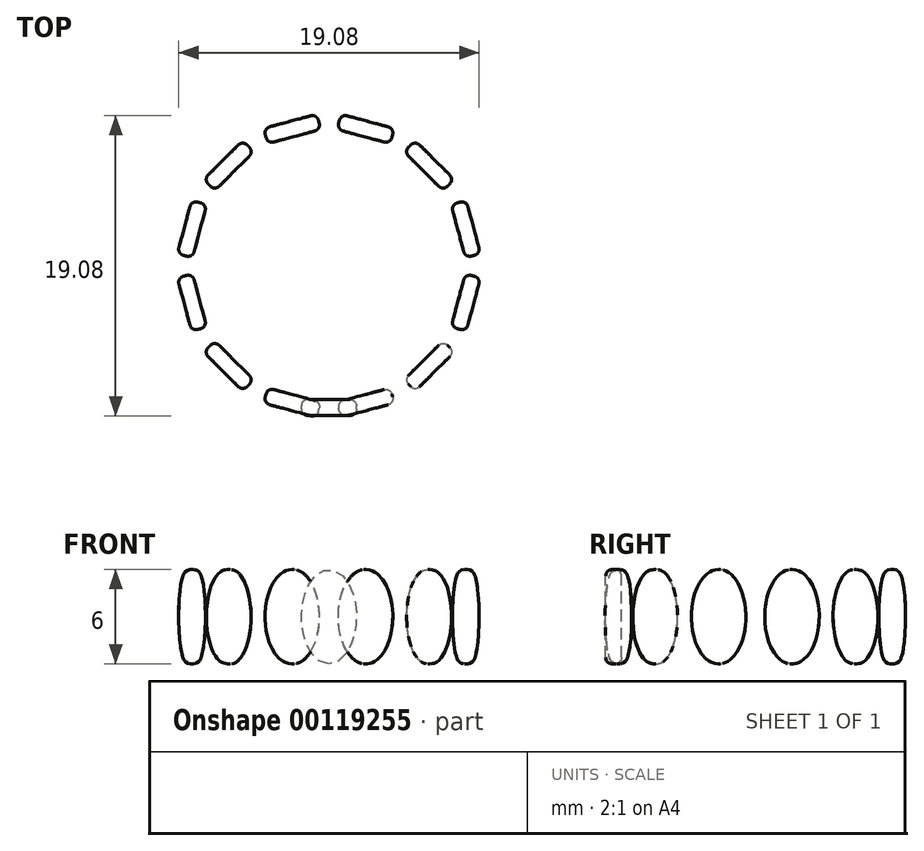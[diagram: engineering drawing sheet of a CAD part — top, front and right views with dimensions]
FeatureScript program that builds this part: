
annotation { "Feature Type Name" : "Feature", "Feature Type Description" : "" }
export const myFeature = defineFeature(function(context is Context, id is Id, definition is map)
    precondition{}
    {
        {
            var Q0;
            Q0=qCreatedBy(makeId("Front.planeOp"),FACE);
            cPlane(context, id + "F0", {"entities" : qUnion([Q0]), "cplaneType" : CPlaneType.OFFSET, "offset" : 8.5 * mm, "width" : 152.4 * mm, "height" : 152.4 * mm});
        }
        {
            var Q0;
            Q0=qCreatedBy(id+"F0.planeOp",FACE);
            var sketch = newSketch(context, id + "F1", { "sketchPlane" : qUnion([Q0])});
            skEllipse(sketch, "E0", {"center": v(0, 0) * mm, "majorRadius": 3 * mm, "minorRadius": 1.75 * mm, "majorAxis": v(0, -1)});
            skFitSpline(sketch, "E1.0", {"points": [v(-0.68, -3.92) * mm, v(0, -4.04) * mm, v(0.68, -3.92) * mm, v(1.27, -3.6) * mm, v(1.74, -3.17) * mm, v(2.12, -2.64) * mm, v(2.4, -2.04) * mm, v(2.6, -1.39) * mm, v(2.72, -0.7) * mm, v(2.76, 0) * mm, v(2.72, 0.7) * mm, v(2.6, 1.39) * mm, v(2.4, 2.04) * mm, v(2.12, 2.64) * mm, v(1.74, 3.17) * mm, v(1.27, 3.6) * mm, v(0.68, 3.92) * mm, v(0, 4.04) * mm, v(-0.68, 3.92) * mm, v(-1.27, 3.6) * mm, v(-1.74, 3.17) * mm, v(-2.12, 2.64) * mm, v(-2.4, 2.04) * mm, v(-2.6, 1.39) * mm, v(-2.72, 0.7) * mm, v(-2.76, 0) * mm, v(-2.72, -0.7) * mm, v(-2.6, -1.39) * mm, v(-2.4, -2.04) * mm, v(-2.12, -2.64) * mm, v(-1.74, -3.17) * mm, v(-1.27, -3.6) * mm, v(-0.68, -3.92) * mm, v(0, -4.04) * mm, v(0.68, -3.92) * mm, v(-0.68, -3.92) * mm]});
            skSolve(sketch);
        }
        {
            var Q0;
            Q0 = qSketchRegion(id + "F1", true);
            extrude(context, id + "F2", {"entities" : qUnion([Q0]), "depth" : 1 * mm});
        }
        {
            var Q0;
            Q0=makeQuery(id+"F2.opExtrude","CAP_EDGE",EDGE,{"disambiguationData":[OSD([sQuery(id+"F1.wireOp",EDGE,"E1.0")])],"isStart":false});
            var Q1;
            Q1=makeQuery(id+"F2.opExtrude","CAP_EDGE",EDGE,{"disambiguationData":[OSD([sQuery(id+"F1.wireOp",EDGE,"E1.0")])],"isStart":true});
            var Q2;
            Q2=makeQuery(id+"F2.opExtrude","CAP_EDGE",EDGE,{"disambiguationData":[OSD([sQuery(id+"F1.wireOp",EDGE,"E0")])],"isStart":true});
            var Q3;
            Q3=makeQuery(id+"F2.opExtrude","CAP_EDGE",EDGE,{"disambiguationData":[OSD([sQuery(id+"F1.wireOp",EDGE,"E0")])],"isStart":false});
            fillet(context, id + "F3", {"entities" : qUnion([Q0, Q1, Q2, Q3]), "radius" : .4 * mm, "tangentPropagation" : true, "allowEdgeOverflow" : false});
        }
        {
            var Q0;
            Q0=qCreatedBy(makeId("Top.planeOp"),FACE);
            var sketch = newSketch(context, id + "F4", { "sketchPlane" : qUnion([Q0])});
            skCircle(sketch, "E2", {"center": v(0, 0) * mm, "radius": 8.5 * mm});
            skSolve(sketch);
        }
        {
            var Q0;
            Q0=qCreatedBy(makeId("Front.planeOp"),FACE);
            var sketch = newSketch(context, id + "F5", { "sketchPlane" : qUnion([Q0])});
            skLineSegment(sketch, "E3", {"start": v(0, 0) * mm, "end": v(0, 12.63) * mm, "construction": true});
            skSolve(sketch);
        }
        {
            var Q0;
            Q0=makeQuery(id+"F2.opExtrude","SWEPT_BODY",BODY,{"disambiguationData":[OSD([sQuery(id+"F1.wireOp",EDGE,"E0"),sQuery(id+"F1.wireOp",EDGE,"E1.0")])]});
            var Q1;
            Q1=sQuery(id+"F4.wireOp",EDGE,"E2");
            circularPattern(context, id + "F6", {"entities" : qUnion([Q0]), "axis" : qUnion([Q1]), "angle" : 15 * degree, "instanceCount" : 2});
        }
        {
            var Q0;
            Q0=qCreatedBy(makeId("Top.planeOp"),FACE);
            var sketch = newSketch(context, id + "F7", { "sketchPlane" : qUnion([Q0])});
            skCircle(sketch, "E4", {"center": v(0, 0) * mm, "radius": 8.5 * mm});
            skSolve(sketch);
        }
        {
            var Q0;
            Q0=makeQuery(id+"F6.opPattern","COPY",BODY,{"derivedFrom":makeQuery(id+"F2.opExtrude","SWEPT_BODY",BODY,{"disambiguationData":[OSD([sQuery(id+"F1.wireOp",EDGE,"E0"),sQuery(id+"F1.wireOp",EDGE,"E1.0")])]}),"instanceName":"1"});
            var Q1;
            Q1=sQuery(id+"F7.wireOp",EDGE,"E4");
            circularPattern(context, id + "F8", {"entities" : qUnion([Q0]), "axis" : qUnion([Q1]), "angle" : 30 * degree, "instanceCount" : 14});
        }
    });
